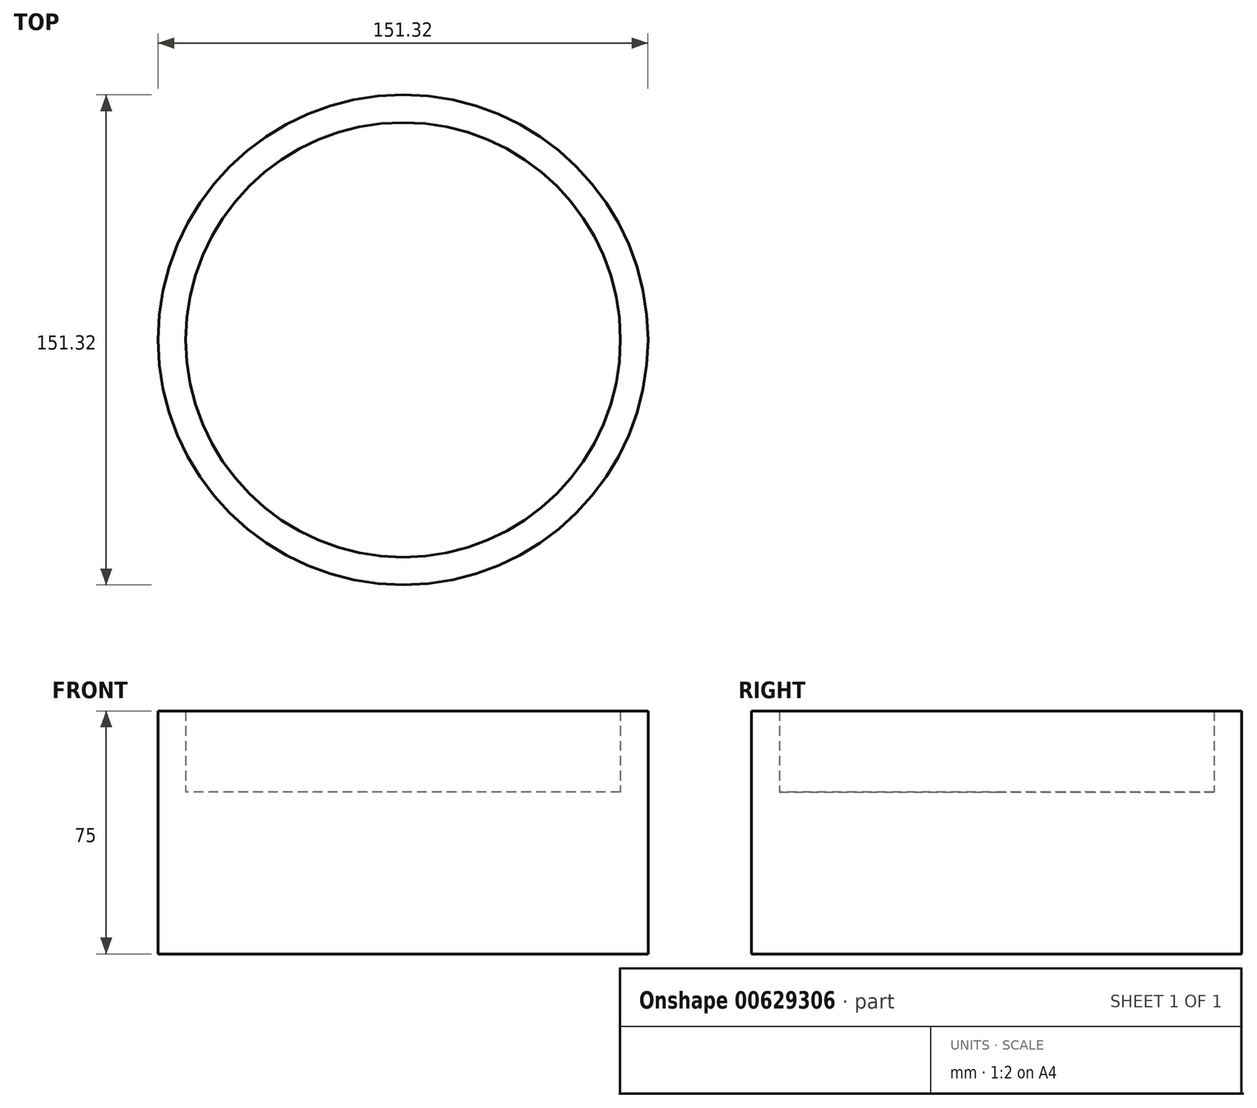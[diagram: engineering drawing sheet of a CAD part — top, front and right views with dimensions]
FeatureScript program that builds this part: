
annotation { "Feature Type Name" : "Feature", "Feature Type Description" : "" }
export const myFeature = defineFeature(function(context is Context, id is Id, definition is map)
    precondition{}
    {
        {
            var Q0;
            Q0=qCreatedBy(makeId("Top.planeOp"),FACE);
            var sketch = newSketch(context, id + "F0", { "sketchPlane" : qUnion([Q0])});
            skCircle(sketch, "E0", {"center": v(0, 0) * mm, "radius": 75.66 * mm});
            skCircle(sketch, "E1", {"center": v(0, 0) * mm, "radius": 67.14 * mm});
            skSolve(sketch);
        }
        {
            var Q0;
            Q0 = qSketchRegion(id + "F0", true);
            extrude(context, id + "F1", {"entities" : qUnion([Q0]), "depth" : 25 * mm, "offsetDistance" : 25 * mm});
        }
        {
            var Q0;
            Q0 = qSketchRegion(id + "F0", true);
            extrude(context, id + "F2", {"entities" : qUnion([Q0]), "operationType" : NewBodyOperationType.ADD, "depth" : 25 * mm, "offsetDistance" : 25 * mm});
        }
        {
            var Q0;
            Q0=makeQuery(id+"F1.opExtrude","CAP_FACE",FACE,{"disambiguationData":[OSD([sQuery(id+"F0.wireOp",EDGE,"E0"),sQuery(id+"F0.wireOp",EDGE,"E1")])],"isStart":true});
            var sketch = newSketch(context, id + "F3", { "sketchPlane" : qUnion([Q0])});
            skCircle(sketch, "E2", {"center": v(0, 0) * mm, "radius": 75.59 * mm});
            skSolve(sketch);
        }
        {
            var Q0;
            Q0=makeQuery(id+"F3.imprint","IMPRINT",FACE,{"disambiguationData":[TD([[makeQuery(id+"F3.imprint","IMPRINT",EDGE,{"derivedFrom":makeQuery(id+"F1.opExtrude","CAP_EDGE",EDGE,{"disambiguationData":[OSD([sQuery(id+"F0.wireOp",EDGE,"E1")])],"isStart":true})}),-1.0]])]});
            var Q1;
            Q1=makeQuery(id+"F3.imprint","IMPRINT",FACE,{"disambiguationData":[TD([[makeQuery(id+"F3.imprint","IMPRINT",EDGE,{"derivedFrom":sQuery(id+"F3.wireOp",EDGE,"E2")}),1.0]])]});
            var Q2;
            Q2=makeQuery(id+"F3.imprint","IMPRINT",FACE,{"disambiguationData":[TD([[makeQuery(id+"F3.imprint","IMPRINT",EDGE,{"derivedFrom":sQuery(id+"F3.wireOp",EDGE,"E2")}),-1.0]])]});
            var Q3;
            Q3=makeQuery(id+"F1.opExtrude","CAP_FACE",FACE,{"disambiguationData":[OSD([sQuery(id+"F0.wireOp",EDGE,"E0"),sQuery(id+"F0.wireOp",EDGE,"E1")])],"isStart":true});
            var Q4;
            Q4=makeQuery(id+"F1.opExtrude","CAP_FACE",FACE,{"disambiguationData":[OSD([sQuery(id+"F0.wireOp",EDGE,"E0"),sQuery(id+"F0.wireOp",EDGE,"E1")])],"isStart":false});
            extrude(context, id + "F4", {"entities" : qUnion([Q0, Q1, Q2, Q3, Q4]), "operationType" : NewBodyOperationType.ADD, "depth" : 50 * mm, "offsetDistance" : 25 * mm});
        }
    });
